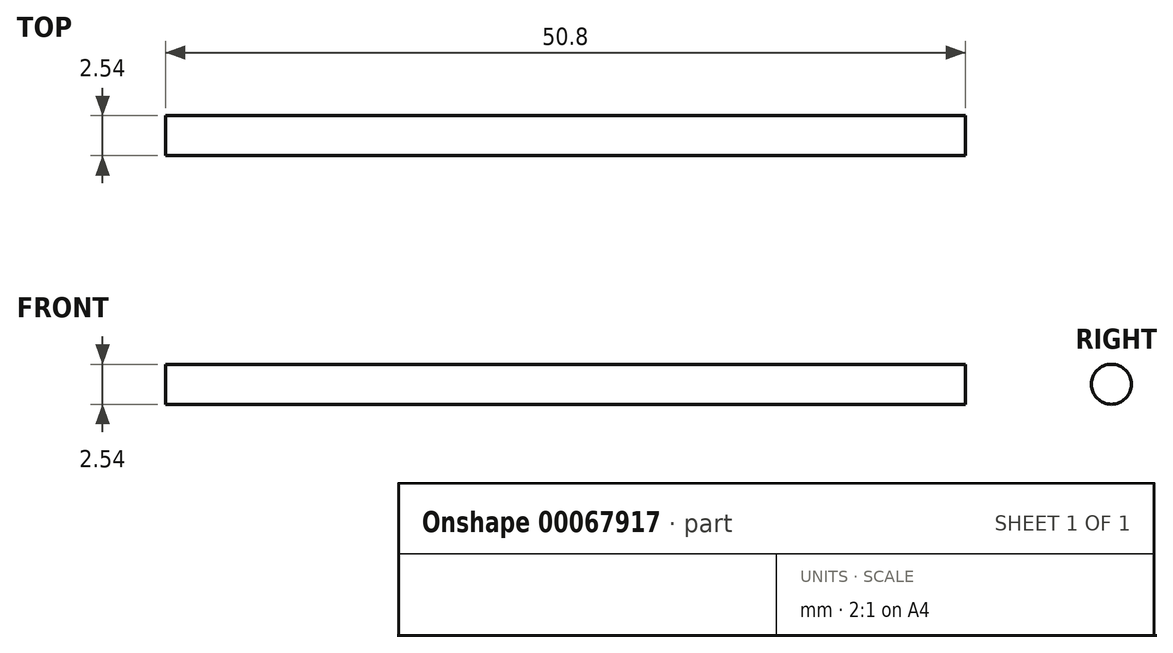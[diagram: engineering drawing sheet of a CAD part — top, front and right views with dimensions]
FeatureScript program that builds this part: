
annotation { "Feature Type Name" : "Feature", "Feature Type Description" : "" }
export const myFeature = defineFeature(function(context is Context, id is Id, definition is map)
    precondition{}
    {
        {
            assignVariable(context, id + "F0", {"name" : "ZPos", "anyValue" : 2});
        }
        {
            var Q0;
            Q0=qCreatedBy(makeId("Top.planeOp"),FACE);
            var sketch = newSketch(context, id + "F1", { "sketchPlane" : qUnion([Q0])});
            skCircle(sketch, "E0.cCircle", {"center": v(0, 0) * mm, "radius": 152.4 * mm, "construction": true});
            skLineSegment(sketch, "E0.0", {"start": v(87.99, 152.4) * mm, "end": v(175.98, 0) * mm});
            skLineSegment(sketch, "E0.1", {"start": v(175.98, 0) * mm, "end": v(87.99, -152.4) * mm});
            skLineSegment(sketch, "E0.2", {"start": v(87.99, -152.4) * mm, "end": v(-87.99, -152.4) * mm});
            skLineSegment(sketch, "E0.3", {"start": v(-87.99, -152.4) * mm, "end": v(-175.98, 0) * mm});
            skLineSegment(sketch, "E0.4", {"start": v(-175.98, 0) * mm, "end": v(-87.99, 152.4) * mm});
            skLineSegment(sketch, "E0.5", {"start": v(-87.99, 152.4) * mm, "end": v(87.99, 152.4) * mm});
            skPoint(sketch, "E0.0.midPoint", {"position": v(131.98, 76.2) * mm});
            skText(sketch, "E1", { "text": "1\n", "fontName": "OpenSans-Regular.ttf"});
            skText(sketch, "E2", { "text": "2\n", "fontName": "OpenSans-Regular.ttf"});
            skText(sketch, "E3", { "text": "3\n", "fontName": "OpenSans-Regular.ttf"});
            const initialGuessF1  = {"E1": [-0.00997, -0.1984, 1, 0, 0.02637], "E2": [0.15081, 0.07402, 1, 0, 0.02748], "E3": [-0.18048, 0.09683, 1, 0, 0.028]};
            skSetInitialGuess(sketch, initialGuessF1);
            skSolve(sketch);
        }
        {
            var Q0;
            Q0=makeQuery(id+"F1.imprint","IMPRINT",FACE,{"disambiguationData":[TD([[makeQuery(id+"F1.imprint","IMPRINT",EDGE,{"derivedFrom":sQuery(id+"F1.wireOp",EDGE,"E0.0")}),-1.0]])]});
            cPlane(context, id + "F2", {"entities" : qUnion([Q0]), "cplaneType" : CPlaneType.OFFSET, "offset" : (getVariable(context, 'ZPos')) * mm, "width" : 152.4 * mm, "height" : 152.4 * mm});
        }
        {
            var Q0;
            Q0=qCreatedBy(id+"F2.planeOp",FACE);
            var sketch = newSketch(context, id + "F3", { "sketchPlane" : qUnion([Q0])});
            skCircle(sketch, "E4.cCircle", {"center": v(-76.2, -76.2) * mm, "radius": 38.1 * mm, "construction": true});
            skLineSegment(sketch, "E4.0", {"start": v(-38.1, -54.2) * mm, "end": v(-38.1, -98.2) * mm});
            skLineSegment(sketch, "E4.1", {"start": v(-38.1, -98.2) * mm, "end": v(-76.2, -120.2) * mm});
            skLineSegment(sketch, "E4.2", {"start": v(-76.2, -120.2) * mm, "end": v(-114.3, -98.2) * mm});
            skLineSegment(sketch, "E4.3", {"start": v(-114.3, -98.2) * mm, "end": v(-114.3, -54.2) * mm});
            skLineSegment(sketch, "E4.4", {"start": v(-114.3, -54.2) * mm, "end": v(-76.2, -32.2) * mm});
            skLineSegment(sketch, "E4.5", {"start": v(-76.2, -32.2) * mm, "end": v(-38.1, -54.2) * mm});
            skPoint(sketch, "E4.0.midPoint", {"position": v(-38.1, -76.2) * mm});
            skSolve(sketch);
        }
        {
            var Q0;
            Q0=makeQuery(id+"F1.imprint","IMPRINT",FACE,{"disambiguationData":[TD([[makeQuery(id+"F1.imprint","IMPRINT",EDGE,{"derivedFrom":sQuery(id+"F1.wireOp",EDGE,"E0.0")}),-1.0]])]});
            var sketch = newSketch(context, id + "F4", { "sketchPlane" : qUnion([Q0])});
            skLineSegment(sketch, "E5", {"start": v(-25.4, -139.7) * mm, "end": v(25.4, -139.7) * mm});
            skLineSegment(sketch, "E6.1.0", {"start": v(133.68, 47.85) * mm, "end": v(108.28, 91.85) * mm});
            skLineSegment(sketch, "E6.2.0", {"start": v(-108.28, 91.85) * mm, "end": v(-133.68, 47.85) * mm});
            skPoint(sketch, "E6.center", {"position": v(0, 0) * mm});
            skSolve(sketch);
        }
        {
            var Q0;
            Q0=sQuery(id+"F4.wireOp",VERTEX,"E5.end");
            var Q1;
            Q1=sQuery(id+"F4.wireOp",EDGE,"E5");
            cPlane(context, id + "F5", {"entities" : qUnion([Q0, Q1]), "cplaneType" : CPlaneType.LINE_POINT, "offset" : 25.4 * mm, "width" : 152.4 * mm, "height" : 152.4 * mm});
        }
        {
            var Q0;
            Q0=qCreatedBy(id+"F5.planeOp",FACE);
            var sketch = newSketch(context, id + "F6", { "sketchPlane" : qUnion([Q0])});
            skCircle(sketch, "E7", {"center": v(-139.7, 1.27) * mm, "radius": 1.27 * mm});
            skSolve(sketch);
        }
        {
            var Q0;
            Q0 = qSketchRegion(id + "F6", true);
            extrude(context, id + "F7", {"entities" : qUnion([Q0]), "oppositeDirection" : true, "depth" : 50.8 * mm});
        }
        {
            var Q0;
            Q0=makeQuery(id+"F1.imprint","IMPRINT",FACE,{"disambiguationData":[TD([[makeQuery(id+"F1.imprint","IMPRINT",EDGE,{"derivedFrom":sQuery(id+"F1.wireOp",EDGE,"E0.0")}),-1.0]])]});
            var sketch = newSketch(context, id + "F8", { "sketchPlane" : qUnion([Q0])});
            skCircle(sketch, "E8", {"center": v(0, -127.2) * mm, "radius": 4.75 * mm});
            skSolve(sketch);
        }
        {
            var Q0;
            Q0=makeQuery(id+"F1.imprint","IMPRINT",FACE,{"disambiguationData":[TD([[makeQuery(id+"F1.imprint","IMPRINT",EDGE,{"derivedFrom":sQuery(id+"F1.wireOp",EDGE,"E0.0")}),-1.0]])]});
            var sketch = newSketch(context, id + "F9", { "sketchPlane" : qUnion([Q0])});
            skLineSegment(sketch, "E9", {"start": v(-4.07, -124.75) * mm, "end": v(-13.82, -140.97) * mm});
            skLineSegment(sketch, "E10", {"start": v(-13.82, -140.97) * mm, "end": v(-76.2, -120.2) * mm});
            skPoint(sketch, "E11.0", {"position": v(0, -127.2) * mm});
            skLineSegment(sketch, "E12", {"start": v(-3.64, -124.15) * mm, "end": v(-28.37, -153.61) * mm, "construction": true});
            skSolve(sketch);
        }
        {
            var Q0;
            Q0=sQuery(id+"F9.wireOp",VERTEX,"E9.start");
            var Q1;
            Q1=sQuery(id+"F9.wireOp",VERTEX,"E9.end");
            var Q2;
            Q2=sQuery(id+"F3.wireOp",VERTEX,"E4.2.start");
            cPlane(context, id + "F10", {"entities" : qUnion([Q0, Q1, Q2]), "cplaneType" : CPlaneType.THREE_POINT, "offset" : 25.4 * mm, "width" : 152.4 * mm, "height" : 152.4 * mm});
        }
    });
